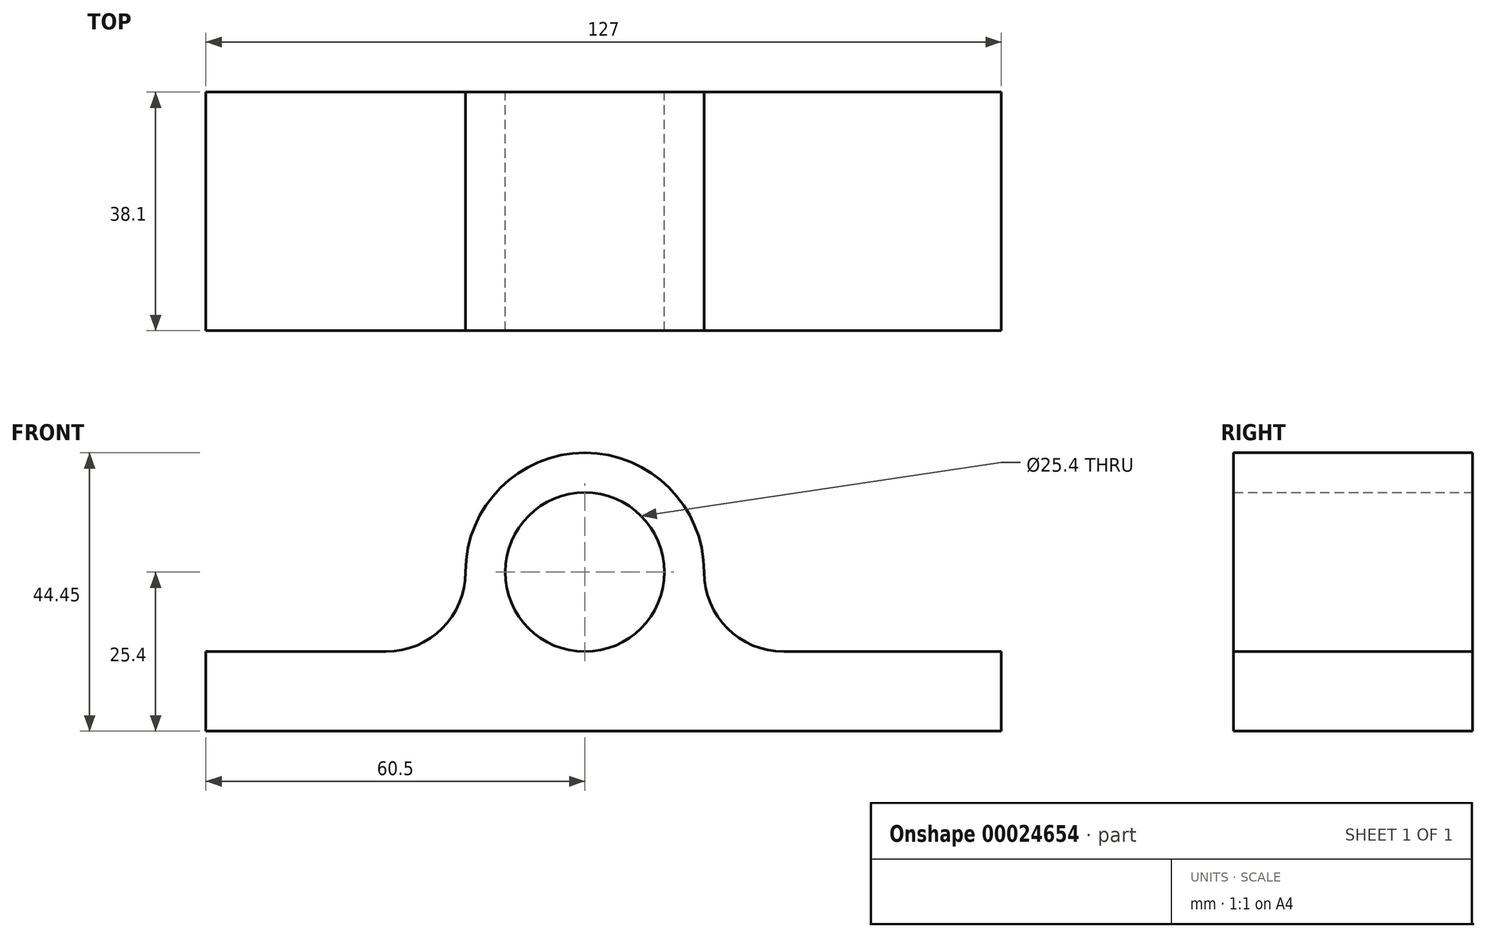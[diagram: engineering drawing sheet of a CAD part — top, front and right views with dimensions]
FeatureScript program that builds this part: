
annotation { "Feature Type Name" : "Feature", "Feature Type Description" : "" }
export const myFeature = defineFeature(function(context is Context, id is Id, definition is map)
    precondition{}
    {
        {
            var Q0;
            Q0=qCreatedBy(makeId("Front.planeOp"),FACE);
            var sketch = newSketch(context, id + "F0", { "sketchPlane" : qUnion([Q0])});
            skLineSegment(sketch, "E0.bottom", {"start": v(-60.5, 19.05) * mm, "end": v(66.5, 19.05) * mm});
            skLineSegment(sketch, "E0.top", {"start": v(-60.5, -25.4) * mm, "end": v(66.5, -25.4) * mm});
            skLineSegment(sketch, "E0.left", {"start": v(-60.5, 19.05) * mm, "end": v(-60.5, -25.4) * mm});
            skLineSegment(sketch, "E0.right", {"start": v(66.5, 19.05) * mm, "end": v(66.5, -25.4) * mm});
            skLineSegment(sketch, "E1.0", {"start": v(-60.5, -12.7) * mm, "end": v(-31.75, -12.7) * mm});
            skCircle(sketch, "E2", {"center": v(0, 0) * mm, "radius": 12.7 * mm});
            skArc(sketch, "E3", {"start": v(19.05, 0) * mm, "mid": v(0, 19.05) * mm, "end": v(-19.05, 0) * mm});
            skLineSegment(sketch, "E4", {"start": v(-19.05, 0) * mm, "end": v(-31.75, 0) * mm, "construction": true});
            skArc(sketch, "E5", {"start": v(-31.75, -12.7) * mm, "mid": v(-22.77, -8.98) * mm, "end": v(-19.05, 0) * mm});
            skLineSegment(sketch, "E6", {"start": v(0, 0) * mm, "end": v(0, -25.4) * mm, "construction": true});
            skArc(sketch, "E7.MirrorCS", {"start": v(31.75, -12.7) * mm, "mid": v(22.77, -8.98) * mm, "end": v(19.05, 0) * mm});
            skLineSegment(sketch, "E8.trimOffspring", {"start": v(31.75, -12.7) * mm, "end": v(66.5, -12.7) * mm});
            skSolve(sketch);
        }
        {
            var Q0;
            {var subQ7=sQuery(id+"F0.wireOp",EDGE,"E0.top");Q0=makeQuery(id+"F0.imprint","IMPRINT",FACE,{"disambiguationData":[TD([[makeQuery(id+"F0.imprint","IMPRINT",EDGE,{"derivedFrom":subQ7}),1.0]])]});}
            extrude(context, id + "F1", {"entities" : qUnion([Q0]), "depth" : 38.1 * mm});
        }
    });
